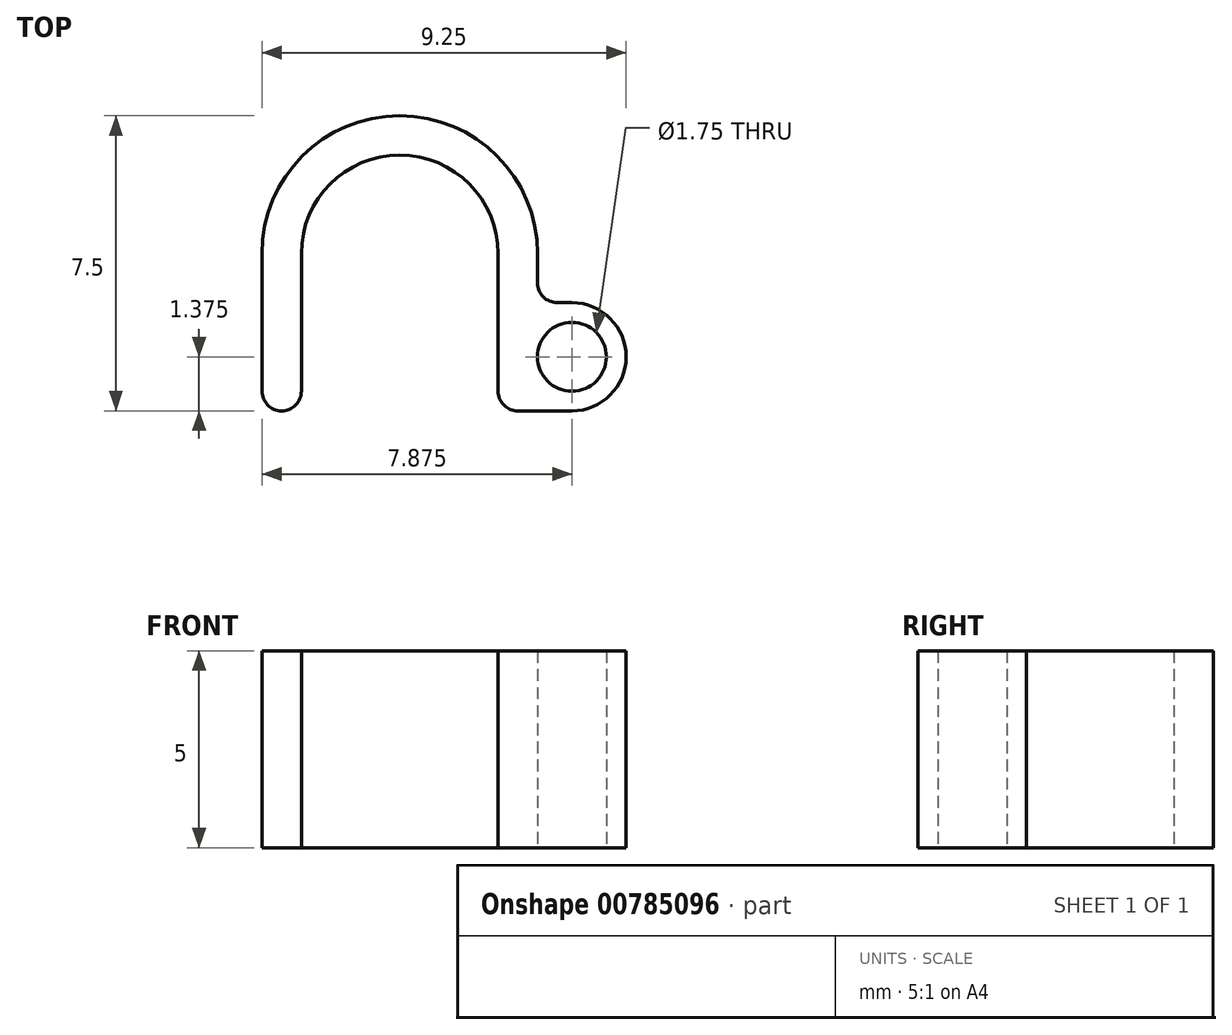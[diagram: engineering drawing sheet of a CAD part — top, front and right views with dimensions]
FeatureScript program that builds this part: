
annotation { "Feature Type Name" : "Feature", "Feature Type Description" : "" }
export const myFeature = defineFeature(function(context is Context, id is Id, definition is map)
    precondition{}
    {
        {
            var Q0;
            Q0=qCreatedBy(makeId("Top.planeOp"),FACE);
            var sketch = newSketch(context, id + "F0", { "sketchPlane" : qUnion([Q0])});
            skArc(sketch, "E0", {"start": v(0, 2.5) * mm, "mid": v(-1.77, 1.77) * mm, "end": v(-2.5, 0) * mm});
            skLineSegment(sketch, "E1", {"start": v(-2.5, 0) * mm, "end": v(-2.5, -3.5) * mm});
            skLineSegment(sketch, "E2", {"start": v(-2.5, -4) * mm, "end": v(-2.5, -4) * mm});
            skLineSegment(sketch, "E3", {"start": v(-2.5, -4) * mm, "end": v(-2.5, 0) * mm});
            skLineSegment(sketch, "E4", {"start": v(0, 4.94) * mm, "end": v(0, -5.84) * mm, "construction": true});
            skPoint(sketch, "E5", {"position": v(0, 2.5) * mm});
            skLineSegment(sketch, "E6", {"start": v(0, 2.5) * mm, "end": v(0, 2.5) * mm});
            skArc(sketch, "E7.MirrorCS", {"start": v(0, 2.5) * mm, "mid": v(1.77, 1.77) * mm, "end": v(2.5, 0) * mm});
            skLineSegment(sketch, "E8.MirrorCS", {"start": v(2.5, -3.5) * mm, "end": v(2.5, 0) * mm});
            skLineSegment(sketch, "E9.MirrorCS", {"start": v(2.5, 0) * mm, "end": v(2.5, -4) * mm});
            skLineSegment(sketch, "E10.MirrorCS", {"start": v(2.5, -4) * mm, "end": v(2.5, -4) * mm});
            skCircle(sketch, "E11", {"center": v(4.38, -2.62) * mm, "radius": 0.88 * mm});
            skArc(sketch, "E12.0", {"start": v(4.38, -4) * mm, "mid": v(5.75, -2.62) * mm, "end": v(4.38, -1.25) * mm});
            skLineSegment(sketch, "E13.0", {"start": v(-3.5, 0) * mm, "end": v(-3.5, -3.5) * mm});
            skArc(sketch, "E13.1", {"start": v(0, 3.5) * mm, "mid": v(-2.47, 2.47) * mm, "end": v(-3.5, 0) * mm});
            skArc(sketch, "E13.2", {"start": v(0, 3.5) * mm, "mid": v(2.47, 2.47) * mm, "end": v(3.5, 0) * mm});
            skLineSegment(sketch, "E13.3", {"start": v(3.5, -0.75) * mm, "end": v(3.5, 0) * mm});
            skLineSegment(sketch, "E14", {"start": v(3.5, -4) * mm, "end": v(3, -4) * mm});
            skLineSegment(sketch, "E15", {"start": v(-3, -4) * mm, "end": v(-3, -4) * mm});
            skLineSegment(sketch, "E16", {"start": v(3.5, -4) * mm, "end": v(4.38, -4) * mm, "construction": true});
            skLineSegment(sketch, "E17", {"start": v(3.5, -4) * mm, "end": v(4.38, -4) * mm});
            skLineSegment(sketch, "E18", {"start": v(4.38, -1.25) * mm, "end": v(4, -1.25) * mm});
            skPoint(sketch, "E19.visualSharp", {"position": v(2.5, -4) * mm});
            skArc(sketch, "E19.filletArc", {"start": v(2.5, -3.5) * mm, "mid": v(2.65, -3.85) * mm, "end": v(3, -4) * mm});
            skPoint(sketch, "E20.visualSharp", {"position": v(3.5, -1.25) * mm});
            skArc(sketch, "E20.filletArc", {"start": v(3.5, -0.75) * mm, "mid": v(3.65, -1.1) * mm, "end": v(4, -1.25) * mm});
            skPoint(sketch, "E21.visualSharp", {"position": v(-2.5, -4) * mm});
            skArc(sketch, "E21.filletArc", {"start": v(-3, -4) * mm, "mid": v(-2.65, -3.85) * mm, "end": v(-2.5, -3.5) * mm});
            skPoint(sketch, "E22.visualSharp", {"position": v(-3.5, -4) * mm});
            skArc(sketch, "E22.filletArc", {"start": v(-3.5, -3.5) * mm, "mid": v(-3.35, -3.85) * mm, "end": v(-3, -4) * mm});
            skSolve(sketch);
        }
        {
            var Q0;
            Q0=makeQuery(id+"F0.imprint","IMPRINT",FACE,{"disambiguationData":[TD([[makeQuery(id+"F0.imprint","IMPRINT",EDGE,{"derivedFrom":sQuery(id+"F0.wireOp",EDGE,"E0")}),-1.0]])]});
            extrude(context, id + "F1", {"entities" : qUnion([Q0]), "depth" : 5 * mm, "offsetDistance" : 25 * mm});
        }
    });
